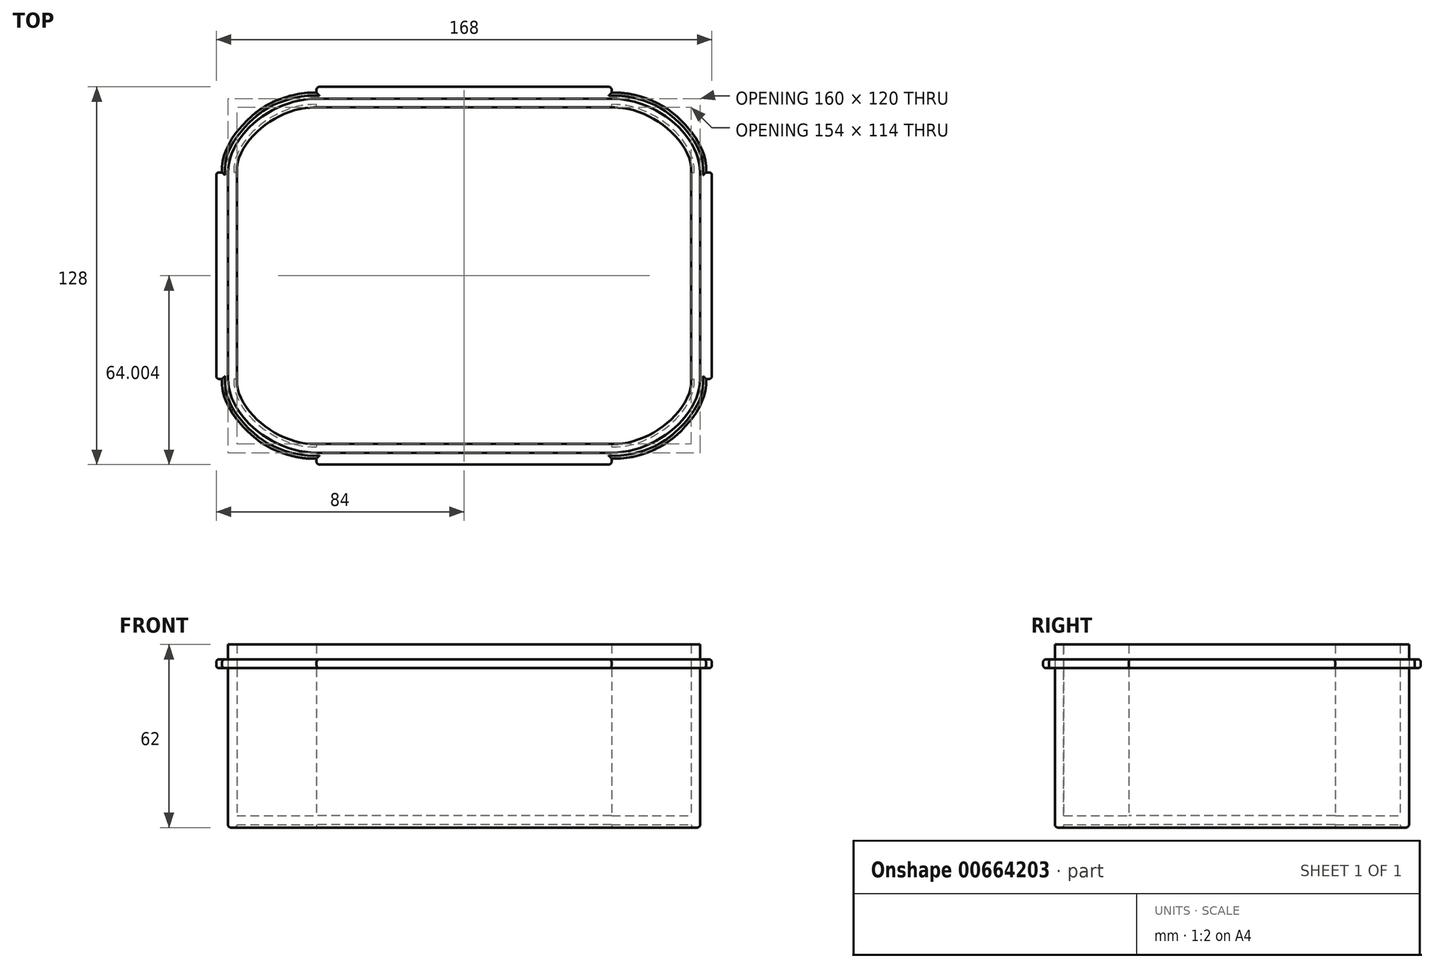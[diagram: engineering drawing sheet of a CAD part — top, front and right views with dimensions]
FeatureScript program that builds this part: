
annotation { "Feature Type Name" : "Feature", "Feature Type Description" : "" }
export const myFeature = defineFeature(function(context is Context, id is Id, definition is map)
    precondition{}
    {
        {
            var Q0;
            Q0=qCreatedBy(makeId("Top.planeOp"),FACE);
            var sketch = newSketch(context, id + "F0", { "sketchPlane" : qUnion([Q0])});
            skLineSegment(sketch, "E0", {"start": v(0, 64.81) * mm, "end": v(-100, 64.81) * mm});
            skLineSegment(sketch, "E1", {"start": v(-100, 64.81) * mm, "end": v(-130, 64.81) * mm, "construction": true});
            skLineSegment(sketch, "E2", {"start": v(-130, 64.81) * mm, "end": v(-130, 39.81) * mm, "construction": true});
            skLineSegment(sketch, "E3", {"start": v(-130, 39.81) * mm, "end": v(-130, -30.19) * mm});
            skLineSegment(sketch, "E4", {"start": v(-130, -30.19) * mm, "end": v(-130, -55.19) * mm, "construction": true});
            skLineSegment(sketch, "E5", {"start": v(-130, -55.19) * mm, "end": v(-100, -55.19) * mm, "construction": true});
            skLineSegment(sketch, "E6", {"start": v(-100, -55.19) * mm, "end": v(0, -55.19) * mm});
            skLineSegment(sketch, "E7", {"start": v(0, 64.81) * mm, "end": v(30, 64.81) * mm, "construction": true});
            skLineSegment(sketch, "E8", {"start": v(30, 64.81) * mm, "end": v(30, 39.81) * mm, "construction": true});
            skLineSegment(sketch, "E9", {"start": v(30, 39.81) * mm, "end": v(30, -30.19) * mm});
            skLineSegment(sketch, "E10", {"start": v(30, -55.19) * mm, "end": v(30, -30.19) * mm, "construction": true});
            skLineSegment(sketch, "E11", {"start": v(30, -55.19) * mm, "end": v(0, -55.19) * mm, "construction": true});
            skFitSpline(sketch, "E12", {"points": [v(-100, -55.19) * mm, v(-130, -30.19) * mm], "startDerivative": vector(-45, 0) * mm, "endDerivative": vector(0, 37.5) * mm});
            skFitSpline(sketch, "E13", {"points": [v(0, -55.19) * mm, v(30, -30.19) * mm], "startDerivative": vector(45, 0) * mm, "endDerivative": vector(0, 37.5) * mm});
            skFitSpline(sketch, "E14", {"points": [v(-130, 39.81) * mm, v(-100, 64.81) * mm], "startDerivative": vector(0, 37.5) * mm, "endDerivative": vector(45, 0) * mm});
            skFitSpline(sketch, "E15", {"points": [v(0, 64.81) * mm, v(30, 39.81) * mm], "startDerivative": vector(45, 0) * mm, "endDerivative": vector(0, -37.5) * mm});
            skLineSegment(sketch, "E16.0", {"start": v(-127, 39.81) * mm, "end": v(-127, -30.19) * mm});
            skFitSpline(sketch, "E16.1", {"points": [v(-100, -52.19) * mm, v(-101.67, -52.19) * mm, v(-105.03, -51.84) * mm, v(-109.98, -50.38) * mm, v(-114.64, -48.1) * mm, v(-118.82, -45.15) * mm, v(-122.32, -41.7) * mm, v(-124.97, -37.92) * mm, v(-126.62, -34.02) * mm, v(-127, -31.45) * mm, v(-127, -30.19) * mm]});
            skFitSpline(sketch, "E16.2", {"points": [v(-127, 39.81) * mm, v(-127, 41.08) * mm, v(-126.62, 43.64) * mm, v(-124.97, 47.55) * mm, v(-122.32, 51.33) * mm, v(-118.82, 54.78) * mm, v(-114.64, 57.73) * mm, v(-109.98, 60) * mm, v(-105.03, 61.47) * mm, v(-101.67, 61.81) * mm, v(-100, 61.81) * mm]});
            skLineSegment(sketch, "E16.3", {"start": v(-100, -52.19) * mm, "end": v(0, -52.19) * mm});
            skLineSegment(sketch, "E16.4", {"start": v(0, 61.81) * mm, "end": v(-100, 61.81) * mm});
            skFitSpline(sketch, "E16.5", {"points": [v(0, 61.81) * mm, v(1.67, 61.81) * mm, v(5.03, 61.47) * mm, v(9.98, 60) * mm, v(14.64, 57.73) * mm, v(18.82, 54.78) * mm, v(22.32, 51.33) * mm, v(24.97, 47.55) * mm, v(26.62, 43.64) * mm, v(27, 41.08) * mm, v(27, 39.81) * mm]});
            skLineSegment(sketch, "E16.6", {"start": v(27, 39.81) * mm, "end": v(27, -30.19) * mm});
            skFitSpline(sketch, "E16.7", {"points": [v(0, -52.19) * mm, v(1.67, -52.19) * mm, v(5.03, -51.84) * mm, v(9.98, -50.38) * mm, v(14.64, -48.1) * mm, v(18.82, -45.15) * mm, v(22.32, -41.7) * mm, v(24.97, -37.92) * mm, v(26.62, -34.02) * mm, v(27, -31.45) * mm, v(27, -30.19) * mm]});
            skSolve(sketch);
        }
        {
            var Q0;
            Q0=makeQuery(id+"F0.imprint","IMPRINT",FACE,{"disambiguationData":[TD([[makeQuery(id+"F0.imprint","IMPRINT",EDGE,{"derivedFrom":sQuery(id+"F0.wireOp",EDGE,"E0")}),1.0]])]});
            extrude(context, id + "F1", {"entities" : qUnion([Q0]), "depth" : 50 * mm, "offsetDistance" : 25 * mm});
        }
        {
            var Q0;
            Q0=makeQuery(id+"F0.imprint","IMPRINT",FACE,{"disambiguationData":[TD([[makeQuery(id+"F0.imprint","IMPRINT",EDGE,{"derivedFrom":sQuery(id+"F0.wireOp",EDGE,"E16.0")}),1.0]])]});
            extrude(context, id + "F2", {"entities" : qUnion([Q0]), "operationType" : NewBodyOperationType.ADD, "oppositeDirection" : true, "depth" : 3 * mm, "offsetDistance" : 25 * mm});
        }
        {
            var Q0;
            Q0=makeQuery(id+"F0.imprint","IMPRINT",FACE,{"disambiguationData":[TD([[makeQuery(id+"F0.imprint","IMPRINT",EDGE,{"derivedFrom":sQuery(id+"F0.wireOp",EDGE,"E0")}),1.0]])]});
            extrude(context, id + "F3", {"entities" : qUnion([Q0]), "operationType" : NewBodyOperationType.ADD, "oppositeDirection" : true, "depth" : 4 * mm, "offsetDistance" : 25 * mm});
        }
        {
            var Q0;
            Q0=makeQuery(id+"F3.opExtrude","CAP_EDGE",EDGE,{"disambiguationData":[OSD([sQuery(id+"F0.wireOp",EDGE,"E16.0")])],"isStart":false});
            var Q1;
            Q1=makeQuery(id+"F3.opExtrude","CAP_EDGE",EDGE,{"disambiguationData":[OSD([sQuery(id+"F0.wireOp",EDGE,"E16.1")])],"isStart":false});
            var Q2;
            Q2=makeQuery(id+"F3.opExtrude","CAP_EDGE",EDGE,{"disambiguationData":[OSD([sQuery(id+"F0.wireOp",EDGE,"E16.2")])],"isStart":false});
            var Q3;
            Q3=makeQuery(id+"F3.opExtrude","CAP_EDGE",EDGE,{"disambiguationData":[OSD([sQuery(id+"F0.wireOp",EDGE,"E16.4")])],"isStart":false});
            var Q4;
            Q4=makeQuery(id+"F3.opExtrude","CAP_EDGE",EDGE,{"disambiguationData":[OSD([sQuery(id+"F0.wireOp",EDGE,"E16.5")])],"isStart":false});
            var Q5;
            Q5=makeQuery(id+"F3.opExtrude","CAP_EDGE",EDGE,{"disambiguationData":[OSD([sQuery(id+"F0.wireOp",EDGE,"E16.6")])],"isStart":false});
            var Q6;
            Q6=makeQuery(id+"F3.opExtrude","CAP_EDGE",EDGE,{"disambiguationData":[OSD([sQuery(id+"F0.wireOp",EDGE,"E16.3")])],"isStart":false});
            var Q7;
            Q7=makeQuery(id+"F3.opExtrude","CAP_EDGE",EDGE,{"disambiguationData":[OSD([sQuery(id+"F0.wireOp",EDGE,"E16.7")])],"isStart":false});
            fillet(context, id + "F4", {"entities" : qUnion([Q0, Q1, Q2, Q3, Q4, Q5, Q6, Q7]), "radius" : 1 * mm, "tangentPropagation" : true, "allowEdgeOverflow" : false});
        }
        {
            var Q0;
            Q0=makeQuery(id+"F1.opExtrude","CAP_FACE",FACE,{"disambiguationData":[OSD([sQuery(id+"F0.wireOp",EDGE,"E0"),sQuery(id+"F0.wireOp",EDGE,"E3"),sQuery(id+"F0.wireOp",EDGE,"E6"),sQuery(id+"F0.wireOp",EDGE,"E9"),sQuery(id+"F0.wireOp",EDGE,"E12"),sQuery(id+"F0.wireOp",EDGE,"E13"),sQuery(id+"F0.wireOp",EDGE,"E14"),sQuery(id+"F0.wireOp",EDGE,"E15"),sQuery(id+"F0.wireOp",EDGE,"E16.0"),sQuery(id+"F0.wireOp",EDGE,"E16.1"),sQuery(id+"F0.wireOp",EDGE,"E16.2"),sQuery(id+"F0.wireOp",EDGE,"E16.3"),sQuery(id+"F0.wireOp",EDGE,"E16.4"),sQuery(id+"F0.wireOp",EDGE,"E16.5"),sQuery(id+"F0.wireOp",EDGE,"E16.6"),sQuery(id+"F0.wireOp",EDGE,"E16.7")])],"isStart":false});
            var sketch = newSketch(context, id + "F5", { "sketchPlane" : qUnion([Q0])});
            skLineSegment(sketch, "E17.1", {"start": v(34, 39.81) * mm, "end": v(34, -30.19) * mm});
            skLineSegment(sketch, "E17.2", {"start": v(0, 68.81) * mm, "end": v(-100, 68.81) * mm});
            skLineSegment(sketch, "E17.5", {"start": v(-134, 39.81) * mm, "end": v(-134, -30.19) * mm});
            skLineSegment(sketch, "E17.7", {"start": v(-100, -59.19) * mm, "end": v(0, -59.19) * mm});
            skLineSegment(sketch, "E18", {"start": v(0, 68.81) * mm, "end": v(0, 66.81) * mm});
            skLineSegment(sketch, "E19", {"start": v(34, 39.81) * mm, "end": v(32, 39.81) * mm});
            skFitSpline(sketch, "E20.0", {"points": [v(0, 66.81) * mm, v(2.01, 66.81) * mm, v(6.02, 66.4) * mm, v(13.73, 64.11) * mm, v(20.66, 60) * mm, v(26.14, 54.6) * mm, v(29.35, 50.04) * mm, v(31.47, 45.07) * mm, v(32, 41.58) * mm, v(32, 39.81) * mm]});
            skLineSegment(sketch, "E21", {"start": v(-100, 68.81) * mm, "end": v(-100, 66.81) * mm});
            skLineSegment(sketch, "E22", {"start": v(-134, 39.81) * mm, "end": v(-132, 39.81) * mm});
            skFitSpline(sketch, "E23.0", {"points": [v(-132, 39.81) * mm, v(-132, 41.58) * mm, v(-131.47, 45.07) * mm, v(-129.35, 50.04) * mm, v(-126.14, 54.6) * mm, v(-120.66, 60) * mm, v(-113.73, 64.11) * mm, v(-106.02, 66.4) * mm, v(-102.01, 66.81) * mm, v(-100, 66.81) * mm]});
            skLineSegment(sketch, "E24", {"start": v(-100, -57.19) * mm, "end": v(-100, -59.19) * mm});
            skLineSegment(sketch, "E25", {"start": v(-134, -30.19) * mm, "end": v(-132, -30.19) * mm});
            skFitSpline(sketch, "E26.0", {"points": [v(-100, -57.19) * mm, v(-102.01, -57.19) * mm, v(-106.02, -56.77) * mm, v(-113.73, -54.48) * mm, v(-120.66, -50.36) * mm, v(-126.14, -44.97) * mm, v(-129.35, -40.41) * mm, v(-131.47, -35.45) * mm, v(-132, -31.95) * mm, v(-132, -30.19) * mm]});
            skLineSegment(sketch, "E27", {"start": v(34, -30.19) * mm, "end": v(32, -30.19) * mm});
            skLineSegment(sketch, "E28", {"start": v(0, -57.19) * mm, "end": v(0, -59.19) * mm});
            skFitSpline(sketch, "E29.0", {"points": [v(0, -57.19) * mm, v(2.01, -57.19) * mm, v(6.02, -56.77) * mm, v(13.73, -54.48) * mm, v(20.66, -50.36) * mm, v(26.14, -44.97) * mm, v(29.35, -40.41) * mm, v(31.47, -35.45) * mm, v(32, -31.95) * mm, v(32, -30.19) * mm]});
            skSolve(sketch);
        }
        {
            var Q0;
            Q0=makeQuery(id+"F5.imprint","IMPRINT",FACE,{"disambiguationData":[TD([[makeQuery(id+"F5.imprint","IMPRINT",EDGE,{"derivedFrom":sQuery(id+"F5.wireOp",EDGE,"E17.0")}),-1.0]])]});
            var Q1;
            {var subQ1=sQuery(id+"F5.wireOp",EDGE,"E17.1");Q1=makeQuery(id+"F5.imprint","IMPRINT",FACE,{"disambiguationData":[TD([[makeQuery(id+"F5.imprint","IMPRINT",EDGE,{"derivedFrom":subQ1}),-1.0]])]});}
            var Q2;
            {var subQ4=sQuery(id+"F5.wireOp",EDGE,"E17.2");Q2=makeQuery(id+"F5.imprint","IMPRINT",FACE,{"disambiguationData":[TD([[makeQuery(id+"F5.imprint","IMPRINT",EDGE,{"derivedFrom":subQ4}),1.0]])]});}
            var Q3;
            {var subQ1=sQuery(id+"F5.wireOp",EDGE,"E17.5");Q3=makeQuery(id+"F5.imprint","IMPRINT",FACE,{"disambiguationData":[TD([[makeQuery(id+"F5.imprint","IMPRINT",EDGE,{"derivedFrom":subQ1}),1.0]])]});}
            var Q4;
            {var subQ4=sQuery(id+"F5.wireOp",EDGE,"E17.7");Q4=makeQuery(id+"F5.imprint","IMPRINT",FACE,{"disambiguationData":[TD([[makeQuery(id+"F5.imprint","IMPRINT",EDGE,{"derivedFrom":subQ4}),1.0]])]});}
            extrude(context, id + "F6", {"entities" : qUnion([Q0, Q1, Q2, Q3, Q4]), "depth" : 3 * mm, "offsetDistance" : 25 * mm});
        }
        {
            var Q0;
            Q0=makeQuery(id+"F1.opExtrude","CAP_FACE",FACE,{"disambiguationData":[OSD([sQuery(id+"F0.wireOp",EDGE,"E0"),sQuery(id+"F0.wireOp",EDGE,"E3"),sQuery(id+"F0.wireOp",EDGE,"E6"),sQuery(id+"F0.wireOp",EDGE,"E9"),sQuery(id+"F0.wireOp",EDGE,"E12"),sQuery(id+"F0.wireOp",EDGE,"E13"),sQuery(id+"F0.wireOp",EDGE,"E14"),sQuery(id+"F0.wireOp",EDGE,"E15"),sQuery(id+"F0.wireOp",EDGE,"E16.0"),sQuery(id+"F0.wireOp",EDGE,"E16.1"),sQuery(id+"F0.wireOp",EDGE,"E16.2"),sQuery(id+"F0.wireOp",EDGE,"E16.3"),sQuery(id+"F0.wireOp",EDGE,"E16.4"),sQuery(id+"F0.wireOp",EDGE,"E16.5"),sQuery(id+"F0.wireOp",EDGE,"E16.6"),sQuery(id+"F0.wireOp",EDGE,"E16.7")])],"isStart":false});
            extrude(context, id + "F7", {"entities" : qUnion([Q0]), "depth" : 8 * mm, "offsetDistance" : 25 * mm});
        }
        {
            var Q0;
            Q0=makeQuery(id+"F6.opExtrude","CAP_EDGE",EDGE,{"disambiguationData":[OSD([sQuery(id+"F5.wireOp",EDGE,"E26.0")])],"isStart":false});
            var Q1;
            Q1=makeQuery(id+"F6.opExtrude","CAP_EDGE",EDGE,{"disambiguationData":[OSD([sQuery(id+"F5.wireOp",EDGE,"E25")])],"isStart":false});
            var Q2;
            Q2=makeQuery(id+"F6.opExtrude","CAP_EDGE",EDGE,{"disambiguationData":[OSD([sQuery(id+"F5.wireOp",EDGE,"E17.5")])],"isStart":false});
            var Q3;
            Q3=makeQuery(id+"F6.opExtrude","CAP_EDGE",EDGE,{"disambiguationData":[OSD([sQuery(id+"F5.wireOp",EDGE,"E17.7")])],"isStart":false});
            var Q4;
            Q4=makeQuery(id+"F6.opExtrude","CAP_EDGE",EDGE,{"disambiguationData":[OSD([sQuery(id+"F5.wireOp",EDGE,"E24")])],"isStart":false});
            var Q5;
            Q5=makeQuery(id+"F6.opExtrude","CAP_EDGE",EDGE,{"disambiguationData":[OSD([sQuery(id+"F5.wireOp",EDGE,"E29.0")])],"isStart":false});
            var Q6;
            Q6=makeQuery(id+"F6.opExtrude","CAP_EDGE",EDGE,{"disambiguationData":[OSD([sQuery(id+"F5.wireOp",EDGE,"E28")])],"isStart":false});
            var Q7;
            Q7=makeQuery(id+"F6.opExtrude","CAP_EDGE",EDGE,{"disambiguationData":[OSD([sQuery(id+"F5.wireOp",EDGE,"E27")])],"isStart":false});
            var Q8;
            Q8=makeQuery(id+"F6.opExtrude","CAP_EDGE",EDGE,{"disambiguationData":[OSD([sQuery(id+"F5.wireOp",EDGE,"E17.1")])],"isStart":false});
            var Q9;
            Q9=makeQuery(id+"F6.opExtrude","CAP_EDGE",EDGE,{"disambiguationData":[OSD([sQuery(id+"F5.wireOp",EDGE,"E20.0")])],"isStart":false});
            var Q10;
            Q10=makeQuery(id+"F6.opExtrude","CAP_EDGE",EDGE,{"disambiguationData":[OSD([sQuery(id+"F5.wireOp",EDGE,"E19")])],"isStart":false});
            var Q11;
            Q11=makeQuery(id+"F6.opExtrude","CAP_EDGE",EDGE,{"disambiguationData":[OSD([sQuery(id+"F5.wireOp",EDGE,"E18")])],"isStart":false});
            var Q12;
            Q12=makeQuery(id+"F6.opExtrude","CAP_EDGE",EDGE,{"disambiguationData":[OSD([sQuery(id+"F5.wireOp",EDGE,"E17.2")])],"isStart":false});
            var Q13;
            Q13=makeQuery(id+"F6.opExtrude","CAP_EDGE",EDGE,{"disambiguationData":[OSD([sQuery(id+"F5.wireOp",EDGE,"E23.0")])],"isStart":false});
            var Q14;
            Q14=makeQuery(id+"F6.opExtrude","CAP_EDGE",EDGE,{"disambiguationData":[OSD([sQuery(id+"F5.wireOp",EDGE,"E21")])],"isStart":false});
            var Q15;
            Q15=makeQuery(id+"F6.opExtrude","CAP_EDGE",EDGE,{"disambiguationData":[OSD([sQuery(id+"F5.wireOp",EDGE,"E22")])],"isStart":false});
            fillet(context, id + "F8", {"entities" : qUnion([Q0, Q1, Q2, Q3, Q4, Q5, Q6, Q7, Q8, Q9, Q10, Q11, Q12, Q13, Q14, Q15]), "radius" : 1 * mm, "tangentPropagation" : true, "allowEdgeOverflow" : false});
        }
        {
            var Q0;
            Q0=makeQuery(id+"F6.opExtrude","SWEPT_EDGE",EDGE,{"disambiguationData":[OSD([sQuery(id+"F5.wireOp",EDGE,"E17.5"),sQuery(id+"F5.wireOp",EDGE,"E25")])]});
            var Q1;
            Q1=makeQuery(id+"F6.opExtrude","SWEPT_EDGE",EDGE,{"disambiguationData":[OSD([sQuery(id+"F5.wireOp",EDGE,"E17.7"),sQuery(id+"F5.wireOp",EDGE,"E24")])]});
            var Q2;
            Q2=makeQuery(id+"F6.opExtrude","SWEPT_EDGE",EDGE,{"disambiguationData":[OSD([sQuery(id+"F5.wireOp",EDGE,"E17.7"),sQuery(id+"F5.wireOp",EDGE,"E28")])]});
            var Q3;
            Q3=makeQuery(id+"F6.opExtrude","SWEPT_EDGE",EDGE,{"disambiguationData":[OSD([sQuery(id+"F5.wireOp",EDGE,"E17.1"),sQuery(id+"F5.wireOp",EDGE,"E27")])]});
            var Q4;
            Q4=makeQuery(id+"F6.opExtrude","SWEPT_EDGE",EDGE,{"disambiguationData":[OSD([sQuery(id+"F5.wireOp",EDGE,"E17.1"),sQuery(id+"F5.wireOp",EDGE,"E19")])]});
            var Q5;
            Q5=makeQuery(id+"F6.opExtrude","SWEPT_EDGE",EDGE,{"disambiguationData":[OSD([sQuery(id+"F5.wireOp",EDGE,"E17.2"),sQuery(id+"F5.wireOp",EDGE,"E18")])]});
            var Q6;
            Q6=makeQuery(id+"F6.opExtrude","SWEPT_EDGE",EDGE,{"disambiguationData":[OSD([sQuery(id+"F5.wireOp",EDGE,"E17.2"),sQuery(id+"F5.wireOp",EDGE,"E21")])]});
            var Q7;
            Q7=makeQuery(id+"F6.opExtrude","SWEPT_EDGE",EDGE,{"disambiguationData":[OSD([sQuery(id+"F5.wireOp",EDGE,"E17.5"),sQuery(id+"F5.wireOp",EDGE,"E22")])]});
            fillet(context, id + "F9", {"entities" : qUnion([Q0, Q1, Q2, Q3, Q4, Q5, Q6, Q7]), "radius" : 1 * mm, "tangentPropagation" : true, "allowEdgeOverflow" : false});
        }
        {
            var Q0;
            Q0=makeQuery(id+"F6.opExtrude","CAP_EDGE",EDGE,{"disambiguationData":[OSD([sQuery(id+"F5.wireOp",EDGE,"E23.0")])],"isStart":true});
            var Q1;
            Q1=makeQuery(id+"F6.opExtrude","CAP_EDGE",EDGE,{"disambiguationData":[OSD([sQuery(id+"F5.wireOp",EDGE,"E17.2")])],"isStart":true});
            var Q2;
            Q2=makeQuery(id+"F6.opExtrude","CAP_EDGE",EDGE,{"disambiguationData":[OSD([sQuery(id+"F5.wireOp",EDGE,"E17.5")])],"isStart":true});
            var Q3;
            Q3=makeQuery(id+"F6.opExtrude","CAP_EDGE",EDGE,{"disambiguationData":[OSD([sQuery(id+"F5.wireOp",EDGE,"E22")])],"isStart":true});
            var Q4;
            {var subQ0=sQuery(id+"F5.wireOp",EDGE,"E21");var subQ1=sQuery(id+"F5.wireOp",EDGE,"E17.2");Q4=makeQuery(id+"F9.opFillet","BLEND_EDGE",EDGE,{"blendedFrom":[makeQuery(id+"F6.opExtrude","SWEPT_EDGE",EDGE,{"disambiguationData":[OSD([subQ1,subQ0])]}),makeQuery(id+"F6.opExtrude","CAP_FACE",FACE,{"disambiguationData":[OSD([sQuery(id+"F0.wireOp",EDGE,"E0"),sQuery(id+"F0.wireOp",EDGE,"E3"),sQuery(id+"F0.wireOp",EDGE,"E6"),sQuery(id+"F0.wireOp",EDGE,"E9"),sQuery(id+"F0.wireOp",EDGE,"E12"),sQuery(id+"F0.wireOp",EDGE,"E13"),sQuery(id+"F0.wireOp",EDGE,"E14"),sQuery(id+"F0.wireOp",EDGE,"E15"),sQuery(id+"F5.wireOp",EDGE,"E17.1"),subQ1,sQuery(id+"F5.wireOp",EDGE,"E17.5"),sQuery(id+"F5.wireOp",EDGE,"E17.7"),sQuery(id+"F5.wireOp",EDGE,"E18"),sQuery(id+"F5.wireOp",EDGE,"E19"),sQuery(id+"F5.wireOp",EDGE,"E20.0"),subQ0,sQuery(id+"F5.wireOp",EDGE,"E22"),sQuery(id+"F5.wireOp",EDGE,"E23.0"),sQuery(id+"F5.wireOp",EDGE,"E24"),sQuery(id+"F5.wireOp",EDGE,"E25"),sQuery(id+"F5.wireOp",EDGE,"E26.0"),sQuery(id+"F5.wireOp",EDGE,"E27"),sQuery(id+"F5.wireOp",EDGE,"E28"),sQuery(id+"F5.wireOp",EDGE,"E29.0")])],"isStart":true})],"blendedInto":[makeQuery(id+"F6.opExtrude","CAP_FACE",FACE,{"disambiguationData":[OSD([sQuery(id+"F0.wireOp",EDGE,"E0"),sQuery(id+"F0.wireOp",EDGE,"E3"),sQuery(id+"F0.wireOp",EDGE,"E6"),sQuery(id+"F0.wireOp",EDGE,"E9"),sQuery(id+"F0.wireOp",EDGE,"E12"),sQuery(id+"F0.wireOp",EDGE,"E13"),sQuery(id+"F0.wireOp",EDGE,"E14"),sQuery(id+"F0.wireOp",EDGE,"E15"),sQuery(id+"F5.wireOp",EDGE,"E17.1"),subQ1,sQuery(id+"F5.wireOp",EDGE,"E17.5"),sQuery(id+"F5.wireOp",EDGE,"E17.7"),sQuery(id+"F5.wireOp",EDGE,"E18"),sQuery(id+"F5.wireOp",EDGE,"E19"),sQuery(id+"F5.wireOp",EDGE,"E20.0"),subQ0,sQuery(id+"F5.wireOp",EDGE,"E22"),sQuery(id+"F5.wireOp",EDGE,"E23.0"),sQuery(id+"F5.wireOp",EDGE,"E24"),sQuery(id+"F5.wireOp",EDGE,"E25"),sQuery(id+"F5.wireOp",EDGE,"E26.0"),sQuery(id+"F5.wireOp",EDGE,"E27"),sQuery(id+"F5.wireOp",EDGE,"E28"),sQuery(id+"F5.wireOp",EDGE,"E29.0")])],"isStart":true})]});}
            var Q5;
            Q5=makeQuery(id+"F6.opExtrude","CAP_EDGE",EDGE,{"disambiguationData":[OSD([sQuery(id+"F5.wireOp",EDGE,"E21")])],"isStart":true});
            var Q6;
            {var subQ0=sQuery(id+"F5.wireOp",EDGE,"E22");var subQ1=sQuery(id+"F5.wireOp",EDGE,"E17.5");Q6=makeQuery(id+"F9.opFillet","BLEND_EDGE",EDGE,{"blendedFrom":[makeQuery(id+"F6.opExtrude","SWEPT_EDGE",EDGE,{"disambiguationData":[OSD([subQ1,subQ0])]}),makeQuery(id+"F6.opExtrude","CAP_FACE",FACE,{"disambiguationData":[OSD([sQuery(id+"F0.wireOp",EDGE,"E0"),sQuery(id+"F0.wireOp",EDGE,"E3"),sQuery(id+"F0.wireOp",EDGE,"E6"),sQuery(id+"F0.wireOp",EDGE,"E9"),sQuery(id+"F0.wireOp",EDGE,"E12"),sQuery(id+"F0.wireOp",EDGE,"E13"),sQuery(id+"F0.wireOp",EDGE,"E14"),sQuery(id+"F0.wireOp",EDGE,"E15"),sQuery(id+"F5.wireOp",EDGE,"E17.1"),sQuery(id+"F5.wireOp",EDGE,"E17.2"),subQ1,sQuery(id+"F5.wireOp",EDGE,"E17.7"),sQuery(id+"F5.wireOp",EDGE,"E18"),sQuery(id+"F5.wireOp",EDGE,"E19"),sQuery(id+"F5.wireOp",EDGE,"E20.0"),sQuery(id+"F5.wireOp",EDGE,"E21"),subQ0,sQuery(id+"F5.wireOp",EDGE,"E23.0"),sQuery(id+"F5.wireOp",EDGE,"E24"),sQuery(id+"F5.wireOp",EDGE,"E25"),sQuery(id+"F5.wireOp",EDGE,"E26.0"),sQuery(id+"F5.wireOp",EDGE,"E27"),sQuery(id+"F5.wireOp",EDGE,"E28"),sQuery(id+"F5.wireOp",EDGE,"E29.0")])],"isStart":true})],"blendedInto":[makeQuery(id+"F6.opExtrude","CAP_FACE",FACE,{"disambiguationData":[OSD([sQuery(id+"F0.wireOp",EDGE,"E0"),sQuery(id+"F0.wireOp",EDGE,"E3"),sQuery(id+"F0.wireOp",EDGE,"E6"),sQuery(id+"F0.wireOp",EDGE,"E9"),sQuery(id+"F0.wireOp",EDGE,"E12"),sQuery(id+"F0.wireOp",EDGE,"E13"),sQuery(id+"F0.wireOp",EDGE,"E14"),sQuery(id+"F0.wireOp",EDGE,"E15"),sQuery(id+"F5.wireOp",EDGE,"E17.1"),sQuery(id+"F5.wireOp",EDGE,"E17.2"),subQ1,sQuery(id+"F5.wireOp",EDGE,"E17.7"),sQuery(id+"F5.wireOp",EDGE,"E18"),sQuery(id+"F5.wireOp",EDGE,"E19"),sQuery(id+"F5.wireOp",EDGE,"E20.0"),sQuery(id+"F5.wireOp",EDGE,"E21"),subQ0,sQuery(id+"F5.wireOp",EDGE,"E23.0"),sQuery(id+"F5.wireOp",EDGE,"E24"),sQuery(id+"F5.wireOp",EDGE,"E25"),sQuery(id+"F5.wireOp",EDGE,"E26.0"),sQuery(id+"F5.wireOp",EDGE,"E27"),sQuery(id+"F5.wireOp",EDGE,"E28"),sQuery(id+"F5.wireOp",EDGE,"E29.0")])],"isStart":true})]});}
            var Q7;
            {var subQ0=sQuery(id+"F5.wireOp",EDGE,"E25");var subQ1=sQuery(id+"F5.wireOp",EDGE,"E17.5");Q7=makeQuery(id+"F9.opFillet","BLEND_EDGE",EDGE,{"blendedFrom":[makeQuery(id+"F6.opExtrude","SWEPT_EDGE",EDGE,{"disambiguationData":[OSD([subQ1,subQ0])]}),makeQuery(id+"F6.opExtrude","CAP_FACE",FACE,{"disambiguationData":[OSD([sQuery(id+"F0.wireOp",EDGE,"E0"),sQuery(id+"F0.wireOp",EDGE,"E3"),sQuery(id+"F0.wireOp",EDGE,"E6"),sQuery(id+"F0.wireOp",EDGE,"E9"),sQuery(id+"F0.wireOp",EDGE,"E12"),sQuery(id+"F0.wireOp",EDGE,"E13"),sQuery(id+"F0.wireOp",EDGE,"E14"),sQuery(id+"F0.wireOp",EDGE,"E15"),sQuery(id+"F5.wireOp",EDGE,"E17.1"),sQuery(id+"F5.wireOp",EDGE,"E17.2"),subQ1,sQuery(id+"F5.wireOp",EDGE,"E17.7"),sQuery(id+"F5.wireOp",EDGE,"E18"),sQuery(id+"F5.wireOp",EDGE,"E19"),sQuery(id+"F5.wireOp",EDGE,"E20.0"),sQuery(id+"F5.wireOp",EDGE,"E21"),sQuery(id+"F5.wireOp",EDGE,"E22"),sQuery(id+"F5.wireOp",EDGE,"E23.0"),sQuery(id+"F5.wireOp",EDGE,"E24"),subQ0,sQuery(id+"F5.wireOp",EDGE,"E26.0"),sQuery(id+"F5.wireOp",EDGE,"E27"),sQuery(id+"F5.wireOp",EDGE,"E28"),sQuery(id+"F5.wireOp",EDGE,"E29.0")])],"isStart":true})],"blendedInto":[makeQuery(id+"F6.opExtrude","CAP_FACE",FACE,{"disambiguationData":[OSD([sQuery(id+"F0.wireOp",EDGE,"E0"),sQuery(id+"F0.wireOp",EDGE,"E3"),sQuery(id+"F0.wireOp",EDGE,"E6"),sQuery(id+"F0.wireOp",EDGE,"E9"),sQuery(id+"F0.wireOp",EDGE,"E12"),sQuery(id+"F0.wireOp",EDGE,"E13"),sQuery(id+"F0.wireOp",EDGE,"E14"),sQuery(id+"F0.wireOp",EDGE,"E15"),sQuery(id+"F5.wireOp",EDGE,"E17.1"),sQuery(id+"F5.wireOp",EDGE,"E17.2"),subQ1,sQuery(id+"F5.wireOp",EDGE,"E17.7"),sQuery(id+"F5.wireOp",EDGE,"E18"),sQuery(id+"F5.wireOp",EDGE,"E19"),sQuery(id+"F5.wireOp",EDGE,"E20.0"),sQuery(id+"F5.wireOp",EDGE,"E21"),sQuery(id+"F5.wireOp",EDGE,"E22"),sQuery(id+"F5.wireOp",EDGE,"E23.0"),sQuery(id+"F5.wireOp",EDGE,"E24"),subQ0,sQuery(id+"F5.wireOp",EDGE,"E26.0"),sQuery(id+"F5.wireOp",EDGE,"E27"),sQuery(id+"F5.wireOp",EDGE,"E28"),sQuery(id+"F5.wireOp",EDGE,"E29.0")])],"isStart":true})]});}
            var Q8;
            Q8=makeQuery(id+"F6.opExtrude","CAP_EDGE",EDGE,{"disambiguationData":[OSD([sQuery(id+"F5.wireOp",EDGE,"E25")])],"isStart":true});
            var Q9;
            Q9=makeQuery(id+"F6.opExtrude","CAP_EDGE",EDGE,{"disambiguationData":[OSD([sQuery(id+"F5.wireOp",EDGE,"E26.0")])],"isStart":true});
            var Q10;
            Q10=makeQuery(id+"F6.opExtrude","CAP_EDGE",EDGE,{"disambiguationData":[OSD([sQuery(id+"F5.wireOp",EDGE,"E24")])],"isStart":true});
            var Q11;
            {var subQ0=sQuery(id+"F5.wireOp",EDGE,"E24");var subQ1=sQuery(id+"F5.wireOp",EDGE,"E17.7");Q11=makeQuery(id+"F9.opFillet","BLEND_EDGE",EDGE,{"blendedFrom":[makeQuery(id+"F6.opExtrude","SWEPT_EDGE",EDGE,{"disambiguationData":[OSD([subQ1,subQ0])]}),makeQuery(id+"F6.opExtrude","CAP_FACE",FACE,{"disambiguationData":[OSD([sQuery(id+"F0.wireOp",EDGE,"E0"),sQuery(id+"F0.wireOp",EDGE,"E3"),sQuery(id+"F0.wireOp",EDGE,"E6"),sQuery(id+"F0.wireOp",EDGE,"E9"),sQuery(id+"F0.wireOp",EDGE,"E12"),sQuery(id+"F0.wireOp",EDGE,"E13"),sQuery(id+"F0.wireOp",EDGE,"E14"),sQuery(id+"F0.wireOp",EDGE,"E15"),sQuery(id+"F5.wireOp",EDGE,"E17.1"),sQuery(id+"F5.wireOp",EDGE,"E17.2"),sQuery(id+"F5.wireOp",EDGE,"E17.5"),subQ1,sQuery(id+"F5.wireOp",EDGE,"E18"),sQuery(id+"F5.wireOp",EDGE,"E19"),sQuery(id+"F5.wireOp",EDGE,"E20.0"),sQuery(id+"F5.wireOp",EDGE,"E21"),sQuery(id+"F5.wireOp",EDGE,"E22"),sQuery(id+"F5.wireOp",EDGE,"E23.0"),subQ0,sQuery(id+"F5.wireOp",EDGE,"E25"),sQuery(id+"F5.wireOp",EDGE,"E26.0"),sQuery(id+"F5.wireOp",EDGE,"E27"),sQuery(id+"F5.wireOp",EDGE,"E28"),sQuery(id+"F5.wireOp",EDGE,"E29.0")])],"isStart":true})],"blendedInto":[makeQuery(id+"F6.opExtrude","CAP_FACE",FACE,{"disambiguationData":[OSD([sQuery(id+"F0.wireOp",EDGE,"E0"),sQuery(id+"F0.wireOp",EDGE,"E3"),sQuery(id+"F0.wireOp",EDGE,"E6"),sQuery(id+"F0.wireOp",EDGE,"E9"),sQuery(id+"F0.wireOp",EDGE,"E12"),sQuery(id+"F0.wireOp",EDGE,"E13"),sQuery(id+"F0.wireOp",EDGE,"E14"),sQuery(id+"F0.wireOp",EDGE,"E15"),sQuery(id+"F5.wireOp",EDGE,"E17.1"),sQuery(id+"F5.wireOp",EDGE,"E17.2"),sQuery(id+"F5.wireOp",EDGE,"E17.5"),subQ1,sQuery(id+"F5.wireOp",EDGE,"E18"),sQuery(id+"F5.wireOp",EDGE,"E19"),sQuery(id+"F5.wireOp",EDGE,"E20.0"),sQuery(id+"F5.wireOp",EDGE,"E21"),sQuery(id+"F5.wireOp",EDGE,"E22"),sQuery(id+"F5.wireOp",EDGE,"E23.0"),subQ0,sQuery(id+"F5.wireOp",EDGE,"E25"),sQuery(id+"F5.wireOp",EDGE,"E26.0"),sQuery(id+"F5.wireOp",EDGE,"E27"),sQuery(id+"F5.wireOp",EDGE,"E28"),sQuery(id+"F5.wireOp",EDGE,"E29.0")])],"isStart":true})]});}
            var Q12;
            Q12=makeQuery(id+"F6.opExtrude","CAP_EDGE",EDGE,{"disambiguationData":[OSD([sQuery(id+"F5.wireOp",EDGE,"E17.7")])],"isStart":true});
            var Q13;
            {var subQ0=sQuery(id+"F5.wireOp",EDGE,"E28");var subQ1=sQuery(id+"F5.wireOp",EDGE,"E17.7");Q13=makeQuery(id+"F9.opFillet","BLEND_EDGE",EDGE,{"blendedFrom":[makeQuery(id+"F6.opExtrude","SWEPT_EDGE",EDGE,{"disambiguationData":[OSD([subQ1,subQ0])]}),makeQuery(id+"F6.opExtrude","CAP_FACE",FACE,{"disambiguationData":[OSD([sQuery(id+"F0.wireOp",EDGE,"E0"),sQuery(id+"F0.wireOp",EDGE,"E3"),sQuery(id+"F0.wireOp",EDGE,"E6"),sQuery(id+"F0.wireOp",EDGE,"E9"),sQuery(id+"F0.wireOp",EDGE,"E12"),sQuery(id+"F0.wireOp",EDGE,"E13"),sQuery(id+"F0.wireOp",EDGE,"E14"),sQuery(id+"F0.wireOp",EDGE,"E15"),sQuery(id+"F5.wireOp",EDGE,"E17.1"),sQuery(id+"F5.wireOp",EDGE,"E17.2"),sQuery(id+"F5.wireOp",EDGE,"E17.5"),subQ1,sQuery(id+"F5.wireOp",EDGE,"E18"),sQuery(id+"F5.wireOp",EDGE,"E19"),sQuery(id+"F5.wireOp",EDGE,"E20.0"),sQuery(id+"F5.wireOp",EDGE,"E21"),sQuery(id+"F5.wireOp",EDGE,"E22"),sQuery(id+"F5.wireOp",EDGE,"E23.0"),sQuery(id+"F5.wireOp",EDGE,"E24"),sQuery(id+"F5.wireOp",EDGE,"E25"),sQuery(id+"F5.wireOp",EDGE,"E26.0"),sQuery(id+"F5.wireOp",EDGE,"E27"),subQ0,sQuery(id+"F5.wireOp",EDGE,"E29.0")])],"isStart":true})],"blendedInto":[makeQuery(id+"F6.opExtrude","CAP_FACE",FACE,{"disambiguationData":[OSD([sQuery(id+"F0.wireOp",EDGE,"E0"),sQuery(id+"F0.wireOp",EDGE,"E3"),sQuery(id+"F0.wireOp",EDGE,"E6"),sQuery(id+"F0.wireOp",EDGE,"E9"),sQuery(id+"F0.wireOp",EDGE,"E12"),sQuery(id+"F0.wireOp",EDGE,"E13"),sQuery(id+"F0.wireOp",EDGE,"E14"),sQuery(id+"F0.wireOp",EDGE,"E15"),sQuery(id+"F5.wireOp",EDGE,"E17.1"),sQuery(id+"F5.wireOp",EDGE,"E17.2"),sQuery(id+"F5.wireOp",EDGE,"E17.5"),subQ1,sQuery(id+"F5.wireOp",EDGE,"E18"),sQuery(id+"F5.wireOp",EDGE,"E19"),sQuery(id+"F5.wireOp",EDGE,"E20.0"),sQuery(id+"F5.wireOp",EDGE,"E21"),sQuery(id+"F5.wireOp",EDGE,"E22"),sQuery(id+"F5.wireOp",EDGE,"E23.0"),sQuery(id+"F5.wireOp",EDGE,"E24"),sQuery(id+"F5.wireOp",EDGE,"E25"),sQuery(id+"F5.wireOp",EDGE,"E26.0"),sQuery(id+"F5.wireOp",EDGE,"E27"),subQ0,sQuery(id+"F5.wireOp",EDGE,"E29.0")])],"isStart":true})]});}
            var Q14;
            Q14=makeQuery(id+"F6.opExtrude","CAP_EDGE",EDGE,{"disambiguationData":[OSD([sQuery(id+"F5.wireOp",EDGE,"E29.0")])],"isStart":true});
            var Q15;
            Q15=makeQuery(id+"F6.opExtrude","CAP_EDGE",EDGE,{"disambiguationData":[OSD([sQuery(id+"F5.wireOp",EDGE,"E28")])],"isStart":true});
            var Q16;
            Q16=makeQuery(id+"F6.opExtrude","CAP_EDGE",EDGE,{"disambiguationData":[OSD([sQuery(id+"F5.wireOp",EDGE,"E27")])],"isStart":true});
            var Q17;
            {var subQ0=sQuery(id+"F5.wireOp",EDGE,"E27");var subQ1=sQuery(id+"F5.wireOp",EDGE,"E17.1");Q17=makeQuery(id+"F9.opFillet","BLEND_EDGE",EDGE,{"blendedFrom":[makeQuery(id+"F6.opExtrude","SWEPT_EDGE",EDGE,{"disambiguationData":[OSD([subQ1,subQ0])]}),makeQuery(id+"F6.opExtrude","CAP_FACE",FACE,{"disambiguationData":[OSD([sQuery(id+"F0.wireOp",EDGE,"E0"),sQuery(id+"F0.wireOp",EDGE,"E3"),sQuery(id+"F0.wireOp",EDGE,"E6"),sQuery(id+"F0.wireOp",EDGE,"E9"),sQuery(id+"F0.wireOp",EDGE,"E12"),sQuery(id+"F0.wireOp",EDGE,"E13"),sQuery(id+"F0.wireOp",EDGE,"E14"),sQuery(id+"F0.wireOp",EDGE,"E15"),subQ1,sQuery(id+"F5.wireOp",EDGE,"E17.2"),sQuery(id+"F5.wireOp",EDGE,"E17.5"),sQuery(id+"F5.wireOp",EDGE,"E17.7"),sQuery(id+"F5.wireOp",EDGE,"E18"),sQuery(id+"F5.wireOp",EDGE,"E19"),sQuery(id+"F5.wireOp",EDGE,"E20.0"),sQuery(id+"F5.wireOp",EDGE,"E21"),sQuery(id+"F5.wireOp",EDGE,"E22"),sQuery(id+"F5.wireOp",EDGE,"E23.0"),sQuery(id+"F5.wireOp",EDGE,"E24"),sQuery(id+"F5.wireOp",EDGE,"E25"),sQuery(id+"F5.wireOp",EDGE,"E26.0"),subQ0,sQuery(id+"F5.wireOp",EDGE,"E28"),sQuery(id+"F5.wireOp",EDGE,"E29.0")])],"isStart":true})],"blendedInto":[makeQuery(id+"F6.opExtrude","CAP_FACE",FACE,{"disambiguationData":[OSD([sQuery(id+"F0.wireOp",EDGE,"E0"),sQuery(id+"F0.wireOp",EDGE,"E3"),sQuery(id+"F0.wireOp",EDGE,"E6"),sQuery(id+"F0.wireOp",EDGE,"E9"),sQuery(id+"F0.wireOp",EDGE,"E12"),sQuery(id+"F0.wireOp",EDGE,"E13"),sQuery(id+"F0.wireOp",EDGE,"E14"),sQuery(id+"F0.wireOp",EDGE,"E15"),subQ1,sQuery(id+"F5.wireOp",EDGE,"E17.2"),sQuery(id+"F5.wireOp",EDGE,"E17.5"),sQuery(id+"F5.wireOp",EDGE,"E17.7"),sQuery(id+"F5.wireOp",EDGE,"E18"),sQuery(id+"F5.wireOp",EDGE,"E19"),sQuery(id+"F5.wireOp",EDGE,"E20.0"),sQuery(id+"F5.wireOp",EDGE,"E21"),sQuery(id+"F5.wireOp",EDGE,"E22"),sQuery(id+"F5.wireOp",EDGE,"E23.0"),sQuery(id+"F5.wireOp",EDGE,"E24"),sQuery(id+"F5.wireOp",EDGE,"E25"),sQuery(id+"F5.wireOp",EDGE,"E26.0"),subQ0,sQuery(id+"F5.wireOp",EDGE,"E28"),sQuery(id+"F5.wireOp",EDGE,"E29.0")])],"isStart":true})]});}
            var Q18;
            Q18=makeQuery(id+"F6.opExtrude","CAP_EDGE",EDGE,{"disambiguationData":[OSD([sQuery(id+"F5.wireOp",EDGE,"E17.1")])],"isStart":true});
            var Q19;
            Q19=makeQuery(id+"F6.opExtrude","CAP_EDGE",EDGE,{"disambiguationData":[OSD([sQuery(id+"F5.wireOp",EDGE,"E20.0")])],"isStart":true});
            fillet(context, id + "F10", {"entities" : qUnion([Q0, Q1, Q2, Q3, Q4, Q5, Q6, Q7, Q8, Q9, Q10, Q11, Q12, Q13, Q14, Q15, Q16, Q17, Q18, Q19]), "radius" : 1 * mm, "tangentPropagation" : true, "allowEdgeOverflow" : false});
        }
        {
            var Q0;
            Q0=makeQuery(id+"F3.opExtrude","CAP_EDGE",EDGE,{"disambiguationData":[OSD([sQuery(id+"F0.wireOp",EDGE,"E15")])],"isStart":false});
            var Q1;
            Q1=makeQuery(id+"F3.opExtrude","CAP_EDGE",EDGE,{"disambiguationData":[OSD([sQuery(id+"F0.wireOp",EDGE,"E9")])],"isStart":false});
            var Q2;
            Q2=makeQuery(id+"F3.opExtrude","CAP_EDGE",EDGE,{"disambiguationData":[OSD([sQuery(id+"F0.wireOp",EDGE,"E0")])],"isStart":false});
            fillet(context, id + "F11", {"entities" : qUnion([Q0, Q1, Q2]), "radius" : 1 * mm, "tangentPropagation" : true, "allowEdgeOverflow" : false});
        }
    });
